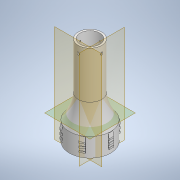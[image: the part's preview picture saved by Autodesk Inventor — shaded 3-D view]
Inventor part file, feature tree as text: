
AUTODESK INVENTOR PART (.ipt)
format: ipt  version: 2022.3 (Build 263350000, 350)  size: 440,832 bytes
history: native  units: mm
features: sketch x8, extrude x5, plane x3, revolve x2, hole x2, mirror x2, pattern_circular x1
ambient origin geometry x8: Origin, YZ Plane, XZ Plane, XY Plane, X Axis, Y Axis, Z Axis, Center Point
bodies: Solid1 (feature_tree)
feature tree (23):
  extrude  "Extrusion1"  Depth=4.0mm
  revolve  "Revolution1"  [1 undecoded]
  plane  "Work Plane1"
  extrude  "Extrusion2"  Depth=100.0mm
  sketch  "Sketch18"  dims[d9=25.0mm d10=100.0mm]
  extrude  "Extrusion11"  Depth=100.0mm
  extrude  "Extrusion12"  Depth=100.0mm
  extrude  "Extrusion13"  [1 undecoded]
  pattern_circular  "Circular Pattern2"  [2 undecoded]
  revolve  "Revolution4"  [1 undecoded]
  plane  "Work Plane3"
  plane  "Work Plane4"
  hole  "Hole5"  [1 undecoded]
  hole  "Hole6"  [1 undecoded]
  mirror  "Mirror1"
  mirror  "Mirror2"
  sketch  "Sketch1"  dims[d0=80.0mm d1=4.0mm]
  sketch  "Sketch2"  dims[d2=40.0mm d3=0.0mm d4=88.0mm]
  sketch  "Sketch3"  dims[d5=50.0mm d8=100.0mm]
  sketch  "Sketch19"  dims[d11=4.0mm d12=100.0mm]
  sketch  "Sketch20"  dims[d13=90.0deg d14=-52.5mm]
  sketch  "Sketch21"  dims[d15=5.0mm]
  sketch  "Sketch22"  dims[d16=65.0mm d17=65.0mm d18=5.0mm d19=15.0mm d20=10.0mm d21=5.0mm d22=0.0mm d79=0.0mm d106=4.0mm d107=10.0mm d108=30.0mm d109=0.0mm d110=10.0mm d111=30.0mm d112=0.0mm d113=1.0mm d114=10.0mm d115=1.0mm d116=3.0mm d117=1.0mm d118=5.0mm d119=1.0mm d120=4.0mm d121=1.0mm d122=5.0mm d123=10.0mm d124=90.0deg d131=10.0mm d132=0.0mm d133=1.0mm d134=3.0mm d135=60.0mm d136=360.0deg d138=2.0mm d139=5.0mm d140=2.0mm d141=5.0mm d142=90.0deg d143=25.0mm d144=25.0mm d145=30.0mm d146=3.4mm d147=6.0mm d148=5.9mm d149=2.0mm d150=90.0deg d151=4.2mm d152=0.0mm d153=30.0mm d154=180.0deg d155=3.4mm d156=6.0mm d157=5.9mm d158=2.0mm d159=90.0deg d160=4.2mm d161=0.0mm d125=0.872665mm d126=0.872665mm d137=14.3117mm]
note: 7 required parameter values undecoded (feature->parameter linkage not recoverable at this tier; creation-order binding heuristic only, values carry confidence <= 0.55)